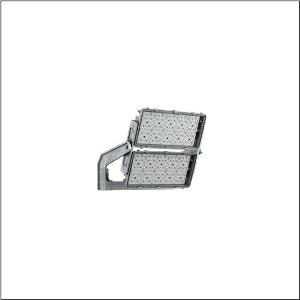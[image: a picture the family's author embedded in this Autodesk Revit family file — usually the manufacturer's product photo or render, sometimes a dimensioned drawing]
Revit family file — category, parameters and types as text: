
# Revit family: floodlight_fl_11_maxi_remote___rs12_5xa779514m01aa_cc46
name_source: partatom
category: Lighting Fixtures
units: mm (PartAtom-declared; Revit-internal decimal feet)

## family parameters
Cut with Voids When Loaded = No
Host = Face
Light Source = No
Part Type = Normal
Room Calculation Point = No
Round Connector Dimension = Use Diameter
Shared = No

## types (1)
- --- (1 x LED, 90180 lm, 916.8 W, 5700K)
    Apparent Load = 917 VA
    CIE Flux Codes = 79 92 99 100 100
    Color Rendering = 90
    Color Temperature = 5700K
    Default Elevation = 1800 mm
    Description = Floodlight FL 11  maxi  Remote floodlight; light control with lens of PMMA; cover panel of toughened safety glass, transparent; light distribution: RS12, rotationally symmetric direct distribution, LEDcolour temperature: 5700K, rated luminous flux: 90.180lm, colour rendering: CRI > 90, light colour: 957; luminous efficacy: 98lm/W; brightness control: DMX+RDM; with terminal, 6-pole, max. 2.5mm², mains connection: 220..240V/380..400V AC, 50/60Hz, surge voltage resistance: line to ground: 10kV, ECG replaceable separately, no afterglow with DALI off / DMX off command, LED unit replaceable without ESD environment, dustproof LED module, dimming range 10..100%; 917W floodlight with 2x LED unit of diecast aluminium, coated grey; length: 713mm / width: 651mm / height: 338mm; mounting bracket, of diecast aluminium, uncoated, natural, equipment: Power, protection rating (complete): IP66; insulation class (complete): insulation class I (protective earthing); certification: CE, ENEC, VDE; ball protection: ball impact resistance with accessories, impact resistance: IK07; rated ambient temperature 10°C, only for outdoor installations, permissible operating ambient temperature: -40..+30°C, permissible storage temperature: -40..+85°C; packaging unit: 1 piece

Light Distribution: RS12
    Height = 320 mm
    Lamp = 1 x LED
    Lamp Light Flux = 90180 lm
    Lamp Power = 916.8 W
    Lamp count = 1
    Length = 712 mm
    Luminous efficacy = 98 lm/W
    Manufacturer = Siteco
    ModVariant = No
    Model = 5XA779514M01AA
    Mounting Place = Ceiling
    Mounting Type = Surface mounted
    Number of Poles = 1
    OnlyDefault = Yes
    Power Factor = 1
    Product Name = Floodlight FL 11 maxi Remote | RS12
    Product group = floodlight | ceiling mounted
    ProductGroupID = 302
    Protection Class = Protection class I
    Protection Degree = IP 66
    RLX_Detail_Level = 1
    RLX_Emergency_Light_Flux = 0 lm
    RLX_Emergency_Type = 0
    RLX_Emergency_Type_DB = No
    RlxData = <blob elided: 41109 chars, md5=9681d91c>
    Socket = socket
    Standby Power = 0 W
    System Light Flux = 90180 lm
    System Power = 917 W
    Type Comments = factory setting: luminous flux: 100 % | dim-lin: 254 | 950 mA
    Type Image = l_1006788.jpg
    URL = http://relux.com
    VarID = @adj_115207
    Voltage = 0 V
    Weight = 0.00 kg
    Width = 655 mm

## geometry (parser evidence)
native form markers: Blend x4, Sweep x10
no freeform markers — native parametric forms only
